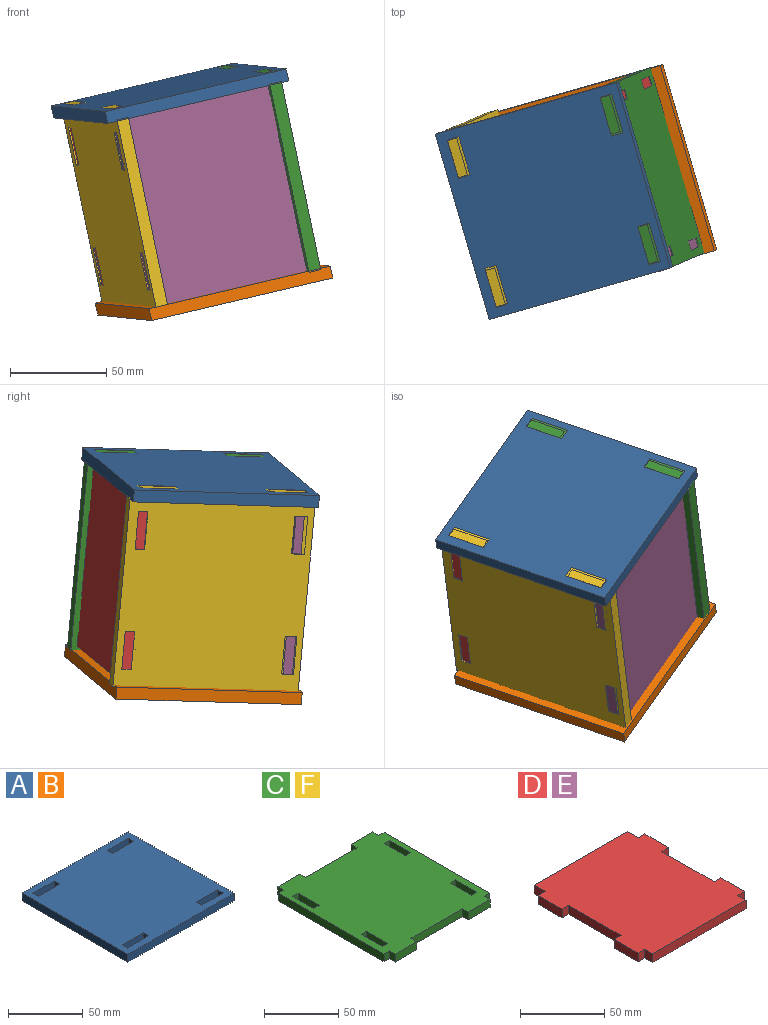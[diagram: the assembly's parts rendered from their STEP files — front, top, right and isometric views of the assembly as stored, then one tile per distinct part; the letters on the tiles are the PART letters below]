
ASSEMBLY  parts=6 mates=5
PART A: 22 faces, bbox 100x100x6.4 mm
  f0: plane 6.35x5.1mm, normal (-1,0,0), area 32.4mm2, adj f1,f19,f20,f21
  f1: plane 20x6.35mm, normal (0,1,0), area 127mm2, adj f0,f2,f20,f21
  f2: plane 6.35x5.1mm, normal (1,0,0), area 32.4mm2, adj f1,f19,f20,f21
  f3: plane 6.35x5.1mm, normal (-1,0,0), area 32.4mm2, adj f4,f15,f20,f21
  f4: plane 20x6.35mm, normal (0,1,0), area 127mm2, adj f3,f5,f20,f21
  f5: plane 6.35x5.1mm, normal (1,0,0), area 32.4mm2, adj f4,f15,f20,f21
  f6: plane 20x6.35mm, normal (0,-1,0), area 127mm2, adj f7,f16,f20,f21
  f7: plane 6.35x5.1mm, normal (-1,0,0), area 32.4mm2, adj f6,f8,f20,f21
  f8: plane 20x6.35mm, normal (0,1,0), area 127mm2, adj f7,f16,f20,f21
  f9: plane 6.35x5.1mm, normal (1,0,0), area 32.4mm2, adj f10,f17,f20,f21
  f10: plane 20x6.35mm, normal (0,-1,0), area 127mm2, adj f9,f11,f20,f21
  f11: plane 6.35x5.1mm, normal (-1,0,0), area 32.4mm2, adj f10,f17,f20,f21
  f12: plane 100x6.35mm, normal (-1,0,0), area 635mm2, adj f13,f18,f20,f21
  f13: plane 100x6.35mm, normal (0,-1,0), area 635mm2, adj f12,f14,f20,f21
  f14: plane 100x6.35mm, normal (1,0,0), area 635mm2, adj f13,f18,f20,f21
  f15: plane 20x6.35mm, normal (0,-1,0), area 127mm2, adj f3,f5,f20,f21
  f16: plane 6.35x5.1mm, normal (1,0,0), area 32.4mm2, adj f6,f8,f20,f21
  f17: plane 20x6.35mm, normal (0,1,0), area 127mm2, adj f9,f11,f20,f21
  f18: plane 100x6.35mm, normal (0,1,0), area 635mm2, adj f12,f14,f20,f21
  f19: plane 20x6.35mm, normal (0,-1,0), area 127mm2, adj f0,f2,f20,f21
  f20: plane 100x100mm, normal (0,0,1), area 9592mm2, adj f0,f1,f2,f3,f4,f5,f6,f7
  f21: plane 100x100mm, normal (0,0,-1), area 9592mm2, adj f0,f1,f2,f3,f4,f5,f6,f7
PART B: same geometry as A
PART C: 38 faces, bbox 100x111.4x6.4 mm
  f0: plane 20x6.35mm, normal (-1,0,0), area 127mm2, adj f1,f35,f36,f37
  f1: plane 6.35x5.1mm, normal (0,1,0), area 32.4mm2, adj f0,f2,f36,f37
  f2: plane 20x6.35mm, normal (1,0,0), area 127mm2, adj f1,f35,f36,f37
  f3: plane 6.35x5.1mm, normal (0,-1,0), area 32.4mm2, adj f4,f31,f36,f37
  f4: plane 20x6.35mm, normal (-1,0,0), area 127mm2, adj f3,f5,f36,f37
  f5: plane 6.35x5.1mm, normal (0,1,0), area 32.4mm2, adj f4,f31,f36,f37
  f6: plane 20x6.35mm, normal (1,0,0), area 127mm2, adj f7,f32,f36,f37
  f7: plane 6.35x5.1mm, normal (0,-1,0), area 32.4mm2, adj f6,f8,f36,f37
  f8: plane 20x6.35mm, normal (-1,0,0), area 127mm2, adj f7,f32,f36,f37
  f9: plane 20x6.35mm, normal (1,0,0), area 127mm2, adj f10,f33,f36,f37
  f10: plane 6.35x5.1mm, normal (0,-1,0), area 32.4mm2, adj f9,f11,f36,f37
  f11: plane 20x6.35mm, normal (-1,0,0), area 127mm2, adj f10,f33,f36,f37
  f12: plane 48.7x6.35mm, normal (0,1,0), area 309.2mm2, adj f13,f34,f36,f37
  f13: plane 6.35x5.7mm, normal (1,0,0), area 36.2mm2, adj f12,f14,f36,f37
  f14: plane 20.7x6.35mm, normal (0,1,0), area 131.4mm2, adj f13,f15,f36,f37
  f15: plane 6.35x5.7mm, normal (-1,0,0), area 36.2mm2, adj f14,f16,f36,f37
  f16: plane 6.35x4.95mm, normal (0,1,0), area 31.4mm2, adj f15,f17,f36,f37
  f17: plane 100x6.35mm, normal (-1,0,0), area 635mm2, adj f16,f18,f36,f37
  f18: plane 6.35x4.95mm, normal (0,-1,0), area 31.4mm2, adj f17,f19,f36,f37
  f19: plane 6.35x5.7mm, normal (-1,0,0), area 36.2mm2, adj f18,f20,f36,f37
  f20: plane 20.7x6.35mm, normal (0,-1,0), area 131.4mm2, adj f19,f21,f36,f37
  f21: plane 6.35x5.7mm, normal (1,0,0), area 36.2mm2, adj f20,f22,f36,f37
  f22: plane 48.7x6.35mm, normal (0,-1,0), area 309.2mm2, adj f21,f23,f36,f37
  f23: plane 6.35x5.7mm, normal (-1,0,0), area 36.2mm2, adj f22,f24,f36,f37
  f24: plane 20.7x6.35mm, normal (0,-1,0), area 131.4mm2, adj f23,f25,f36,f37
  f25: plane 6.35x5.7mm, normal (1,0,0), area 36.2mm2, adj f24,f26,f36,f37
  f26: plane 6.35x4.95mm, normal (0,-1,0), area 31.4mm2, adj f25,f27,f36,f37
  f27: plane 100x6.35mm, normal (1,0,0), area 635mm2, adj f26,f28,f36,f37
  f28: plane 6.35x4.95mm, normal (0,1,0), area 31.4mm2, adj f27,f29,f36,f37
  f29: plane 6.35x5.7mm, normal (1,0,0), area 36.2mm2, adj f28,f30,f36,f37
  f30: plane 20.7x6.35mm, normal (0,1,0), area 131.4mm2, adj f29,f34,f36,f37
  f31: plane 20x6.35mm, normal (1,0,0), area 127mm2, adj f3,f5,f36,f37
  f32: plane 6.35x5.1mm, normal (0,1,0), area 32.4mm2, adj f6,f8,f36,f37
  f33: plane 6.35x5.1mm, normal (0,1,0), area 32.4mm2, adj f9,f11,f36,f37
  f34: plane 6.35x5.7mm, normal (-1,0,0), area 36.2mm2, adj f12,f30,f36,f37
  f35: plane 6.35x5.1mm, normal (0,-1,0), area 32.4mm2, adj f0,f2,f36,f37
  f36: plane 111.4x100mm, normal (0,0,1), area 10064mm2, adj f0,f1,f2,f3,f4,f5,f6,f7
  f37: plane 111.4x100mm, normal (0,0,-1), area 10064mm2, adj f0,f1,f2,f3,f4,f5,f6,f7
PART D: 22 faces, bbox 89.6x100x6.4 mm
  f0: plane 78.18x6.35mm, normal (0,1,0), area 496.5mm2, adj f1,f19,f20,f21
  f1: plane 9.29x6.35mm, normal (-1,0,0), area 59mm2, adj f0,f2,f20,f21
  f2: plane 6.35x5.7mm, normal (0,1,0), area 36.2mm2, adj f1,f3,f20,f21
  f3: plane 20x6.35mm, normal (-1,0,0), area 127mm2, adj f2,f4,f20,f21
  f4: plane 6.35x5.7mm, normal (0,-1,0), area 36.2mm2, adj f3,f5,f20,f21
  f5: plane 43.85x6.35mm, normal (-1,0,0), area 278.5mm2, adj f4,f6,f20,f21
  f6: plane 6.35x5.7mm, normal (0,1,0), area 36.2mm2, adj f5,f7,f20,f21
  f7: plane 20x6.35mm, normal (-1,0,0), area 127mm2, adj f6,f8,f20,f21
  f8: plane 6.35x5.7mm, normal (0,-1,0), area 36.2mm2, adj f7,f9,f20,f21
  f9: plane 6.86x6.35mm, normal (-1,0,0), area 43.5mm2, adj f8,f10,f20,f21
  f10: plane 78.18x6.35mm, normal (0,-1,0), area 496.5mm2, adj f9,f11,f20,f21
  f11: plane 6.86x6.35mm, normal (1,0,0), area 43.5mm2, adj f10,f12,f20,f21
  f12: plane 6.35x5.7mm, normal (0,-1,0), area 36.2mm2, adj f11,f13,f20,f21
  f13: plane 20x6.35mm, normal (1,0,0), area 127mm2, adj f12,f14,f20,f21
  f14: plane 6.35x5.7mm, normal (0,1,0), area 36.2mm2, adj f13,f15,f20,f21
  f15: plane 43.85x6.35mm, normal (1,0,0), area 278.5mm2, adj f14,f16,f20,f21
  f16: plane 6.35x5.7mm, normal (0,-1,0), area 36.2mm2, adj f15,f17,f20,f21
  f17: plane 20x6.35mm, normal (1,0,0), area 127mm2, adj f16,f18,f20,f21
  f18: plane 6.35x5.7mm, normal (0,1,0), area 36.2mm2, adj f17,f19,f20,f21
  f19: plane 9.29x6.35mm, normal (1,0,0), area 59mm2, adj f0,f18,f20,f21
  f20: plane 100x89.58mm, normal (0,0,1), area 8274.4mm2, adj f0,f1,f2,f3,f4,f5,f6,f7
  f21: plane 100x89.58mm, normal (0,0,-1), area 8274.4mm2, adj f0,f1,f2,f3,f4,f5,f6,f7
PART E: same geometry as D
PART F: same geometry as C
PLACE A rot(axis=(0.6,0.8,0.1),173.7deg) t=(-943.45,852.76,564.42)mm
PLACE B rot(axis=(-0.07,-0.12,0.99),106.6deg) t=(-909.14,865.23,458.47)mm
PLACE C rot(axis=(-0.5,-0.68,0.53),134.9deg) t=(-908.34,860.39,638.87)mm
PLACE D rot(axis=(0.17,-0.67,-0.72),177.5deg) t=(-794.19,942.22,425.59)mm
PLACE E rot(axis=(-0.02,0.73,-0.69),159.9deg) t=(-820.61,844.09,655.73)mm
PLACE F rot(axis=(-0.5,-0.68,0.53),134.9deg) t=(-987.61,838.56,620.31)mm
MATE fastened C.f37 <-> B.f1  axis (0.94,0.27,0.22) through (-882.14,909.34,468.13)mm
MATE fastened C.f36 <-> A.f17  axis (-0.94,-0.27,-0.22) through (-891.38,831.15,573.34)mm
MATE fastened F.f36 <-> A.f1  axis (-0.94,-0.27,-0.22) through (-990.07,875.91,556.78)mm
MATE fastened E.f1 <-> C.f36  axis (0.94,0.27,0.22) through (-868.55,828.81,479.01)mm
MATE fastened D.f11 <-> F.f37  axis (-0.94,-0.27,-0.22) through (-967.64,897.07,464.51)mm
